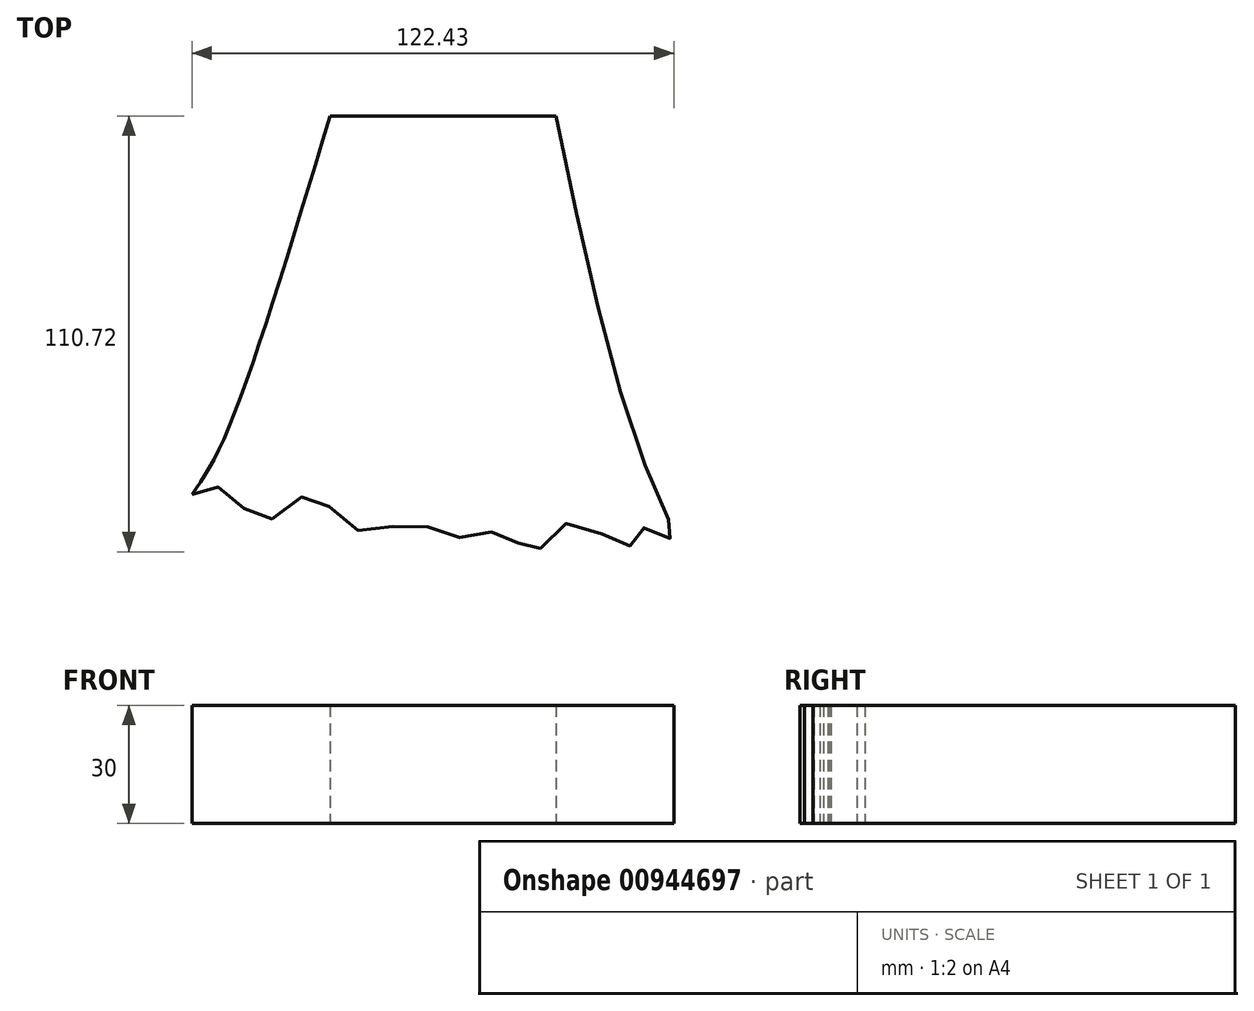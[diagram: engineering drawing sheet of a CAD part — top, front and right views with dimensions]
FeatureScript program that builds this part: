
annotation { "Feature Type Name" : "Feature", "Feature Type Description" : "" }
export const myFeature = defineFeature(function(context is Context, id is Id, definition is map)
    precondition{}
    {
        {
            var Q0;
            Q0=qCreatedBy(makeId("Top.planeOp"),FACE);
            var sketch = newSketch(context, id + "F0", { "sketchPlane" : qUnion([Q0])});
            skFitSpline(sketch, "E0", {"points": [v(-63.67, -19.53) * mm, v(-55.6, -18.1) * mm, v(-45.14, -26.18) * mm, v(-33.74, -19.53) * mm, v(-22.33, -28.32) * mm, v(-7.84, -26.9) * mm, v(4.75, -30.46) * mm, v(15.68, -29.27) * mm, v(23.28, -34.02) * mm, v(33.02, -26.42) * mm, v(47.04, -32.83) * mm, v(50.6, -28.08) * mm, v(58.2, -30.7) * mm, v(52.03, -13.35) * mm, v(28.78, 76.67) * mm], "startDerivative": vector(153.73, 80.82) * mm, "endDerivative": vector(-121.16, 573.46) * mm});
            skFitSpline(sketch, "E1", {"points": [v(-63.67, -19.53) * mm, v(-55.62, -5.48) * mm, v(-28.57, 76.67) * mm], "startDerivative": vector(24.86, 35.76) * mm, "endDerivative": vector(42.97, 142.54) * mm});
            skLineSegment(sketch, "E2", {"start": v(-28.57, 76.67) * mm, "end": v(28.78, 76.67) * mm});
            skSolve(sketch);
        }
        {
            var Q0;
            Q0=makeQuery(id+"F0.imprint","IMPRINT",FACE,{"disambiguationData":[TD([[makeQuery(id+"F0.imprint","IMPRINT",EDGE,{"derivedFrom":sQuery(id+"F0.wireOp",EDGE,"E0")}),1.0]])]});
            extrude(context, id + "F1", {"entities" : qUnion([Q0]), "depth" : 30 * mm, "offsetDistance" : 25.4 * mm});
        }
    });
